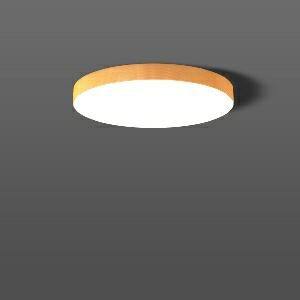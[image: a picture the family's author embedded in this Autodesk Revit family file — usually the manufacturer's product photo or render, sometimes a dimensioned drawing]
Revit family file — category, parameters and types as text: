
# Revit family: flatliner_slim_312283_002_1_76_96d1
name_source: partatom
category: Lighting Fixtures
units: mm (PartAtom-declared; Revit-internal decimal feet)

## family parameters
Cut with Voids When Loaded = No
Host = Face
Light Source = No
Part Type = Normal
Room Calculation Point = No
Round Connector Dimension = Use Diameter
Shared = No

## types (1)
- 982557.002 (1 x LED Modul 840, 2400 lm, 4000)
    Apparent Load = 31 VA
    CIE Flux Codes = 45 76 94 95 100
    Color Rendering = 80
    Color Temperature = 4000
    Default Elevation = 1800 mm
    Description = Series: FLATLINER SLIM
Decorative ceiling luminaire for interior decoration. Base luminaire prepared for the installation of fabric lampshade. Base: metal, white, powder-coated. TouchDim sensor capable. Light and/or presence sensors can be integrated. Modular design: with the basic luminaire, a cylindrical fabric lampshade with a polycarbonate satin-finish diffuser must always be ordered separately. Fabric lampshade and diffuser can be assembled without the use of tools. 
Colour: white
Diameter: 418 mm
Height: 34 mm
Lamp: LED exchangeable
Socket: without socket
Colour temperature: 4000K
Colour rendering index (CRI): 83
System power: 31 W
Rated luminous flux: 2400 lm
Beam angle Down: 117°
Luminous efficiency: 77 lm/W
Control gear: AC power, DALI dimmable
Protection class: I
Type of protection: IP 20
    Height = 34 mm  [stored 0.111549 ft]
    Lamp = 1 x LED Modul 840
    Lamp Light Flux = 2400 lm
    Lamp count = 1
    Length = 418 mm
    Lifetime = 50000 h
    Luminous efficacy = 77 lm/W
    Manufacturer = RZB
    ModVariant = No
    Model = 312283.002.1.76
    Mounting Place = Ceiling
    Mounting Type = Surface mounted
    Number of Poles = 1
    OnlyDefault = Yes
    Power Factor = 1
    Product Name = FLATLINER SLIM
    Product group = Surface mounted ceiling Fabric lampshade luminaires
    ProductGroupID = 313
    Protection Class = Protection class I
    Protection Degree = IP 20
    RLX_Detail_Level = 1
    RLX_Emergency_Light_Flux = 0 lm
    RLX_Emergency_Type = 0
    RLX_Emergency_Type_DB = No
    RlxData = <blob elided: 25413 chars, md5=bd634806>
    Socket = socket
    Standby Power = 0 W
    System Light Flux = 2400 lm
    System Power = 31 W
    Type Image = 312287.002_982442.0063_982444.002.jpg
    URL = http://relux.com
    VarID = 982557_002_b87f
    Voltage = 230 V
    Voltage Range = 220-240 V
    Weight = 0.00 kg
    Width = 0 mm  [stored 0 ft]

note: [stored X ft] marks values corroborated as IEEE doubles in the binary element streams (Revit-internal decimal feet)

## geometry (parser evidence)
native form markers: Blend x4, Sweep x11
no freeform markers — native parametric forms only
